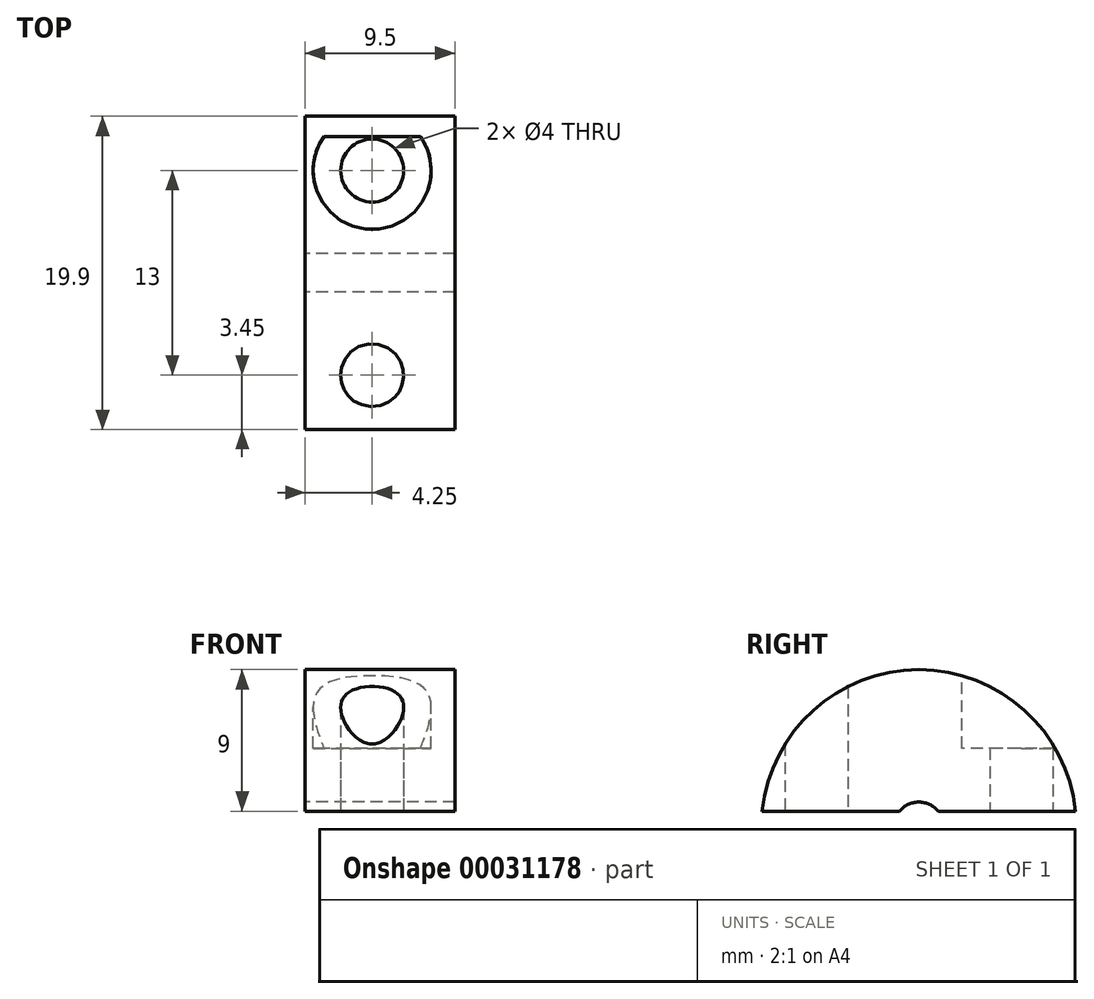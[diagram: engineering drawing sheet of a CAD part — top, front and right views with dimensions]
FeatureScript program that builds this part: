
annotation { "Feature Type Name" : "Feature", "Feature Type Description" : "" }
export const myFeature = defineFeature(function(context is Context, id is Id, definition is map)
    precondition{}
    {
        {
            var Q0;
            Q0=qCreatedBy(makeId("Right.planeOp"),FACE);
            var sketch = newSketch(context, id + "F0", { "sketchPlane" : qUnion([Q0])});
            skArc(sketch, "E0", {"start": v(9.95, 1) * mm, "mid": v(0, 10) * mm, "end": v(-9.95, 1) * mm});
            skLineSegment(sketch, "E1", {"start": v(-9.95, 1) * mm, "end": v(-1.23, 1) * mm});
            skArc(sketch, "E2", {"start": v(1.23, 1) * mm, "mid": v(0, 1.59) * mm, "end": v(-1.23, 1) * mm});
            skLineSegment(sketch, "E3.trimOffspring", {"start": v(1.23, 1) * mm, "end": v(9.95, 1) * mm});
            skSolve(sketch);
        }
        {
            var Q0;
            Q0 = qSketchRegion(id + "F0", true);
            extrude(context, id + "F1", {"entities" : qUnion([Q0]), "depth" : (8.5 + 1) * mm});
        }
        {
            var Q0;
            Q0=makeQuery(id+"F1.opExtrude","SWEPT_FACE",FACE,{"disambiguationData":[OSD([sQuery(id+"F0.wireOp",EDGE,"E1")])]});
            var sketch = newSketch(context, id + "F2", { "sketchPlane" : qUnion([Q0])});
            skCircle(sketch, "E4", {"center": v(4.25, 6.5) * mm, "radius": 2 * mm});
            skCircle(sketch, "E5", {"center": v(4.25, -6.5) * mm, "radius": 2 * mm});
            skLineSegment(sketch, "E6", {"start": v(4.25, 6.5) * mm, "end": v(4.25, -6.5) * mm, "construction": true});
            skLineSegment(sketch, "E7", {"start": v(4.25, 0) * mm, "end": v(0, 0) * mm, "construction": true});
            skPoint(sketch, "E7.endSnap0", {"position": v(0, 5.6) * mm});
            skLineSegment(sketch, "E8", {"start": v(0, 1.23) * mm, "end": v(0, -1.23) * mm, "construction": true});
            skSolve(sketch);
        }
        {
            var Q0;
            Q0 = qSketchRegion(id + "F2", true);
            extrude(context, id + "F3", {"entities" : qUnion([Q0]), "operationType" : NewBodyOperationType.REMOVE, "endBound" : BoundingType.THROUGH_ALL, "oppositeDirection" : true, "depth" : 25 * mm});
        }
        {
            var Q0;
            Q0=qCreatedBy(makeId("Top.planeOp"),FACE);
            cPlane(context, id + "F4", {"entities" : qUnion([Q0]), "cplaneType" : CPlaneType.OFFSET, "offset" : 10 * mm, "width" : 150 * mm, "height" : 150 * mm});
        }
        {
            var Q0;
            Q0=qCreatedBy(id+"F4.planeOp",FACE);
            var sketch = newSketch(context, id + "F5", { "sketchPlane" : qUnion([Q0])});
            skCircle(sketch, "E9", {"center": v(4.25, 6.5) * mm, "radius": 3.75 * mm});
            skSolve(sketch);
        }
        {
            var Q0;
            Q0 = qSketchRegion(id + "F5", true);
            extrude(context, id + "F6", {"entities" : qUnion([Q0]), "operationType" : NewBodyOperationType.REMOVE, "oppositeDirection" : true, "depth" : 5 * mm});
        }
    });
